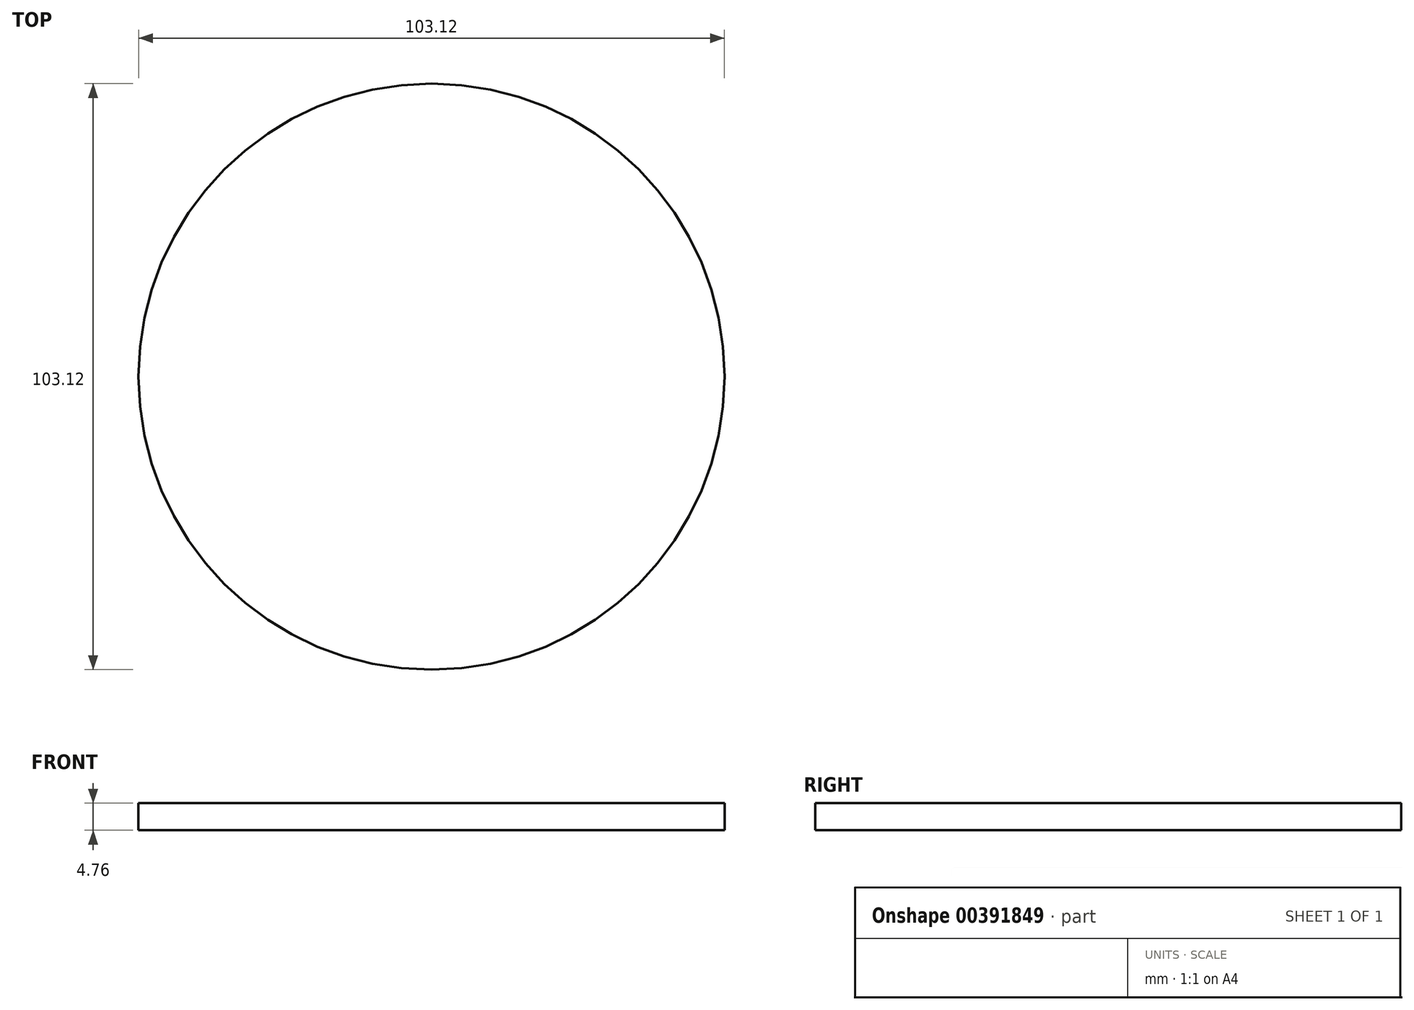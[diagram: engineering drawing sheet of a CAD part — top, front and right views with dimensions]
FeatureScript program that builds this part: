
annotation { "Feature Type Name" : "Feature", "Feature Type Description" : "" }
export const myFeature = defineFeature(function(context is Context, id is Id, definition is map)
    precondition{}
    {
        {
            var Q0;
            Q0=qCreatedBy(makeId("Top.planeOp"),FACE);
            var sketch = newSketch(context, id + "F0", { "sketchPlane" : qUnion([Q0])});
            skCircle(sketch, "E0", {"center": v(0, 0) * mm, "radius": 51.56 * mm});
            skSolve(sketch);
        }
        {
            var Q0;
            Q0 = qSketchRegion(id + "F0", true);
            extrude(context, id + "F1", {"entities" : qUnion([Q0]), "depth" : 4.76 * mm});
        }
    });
